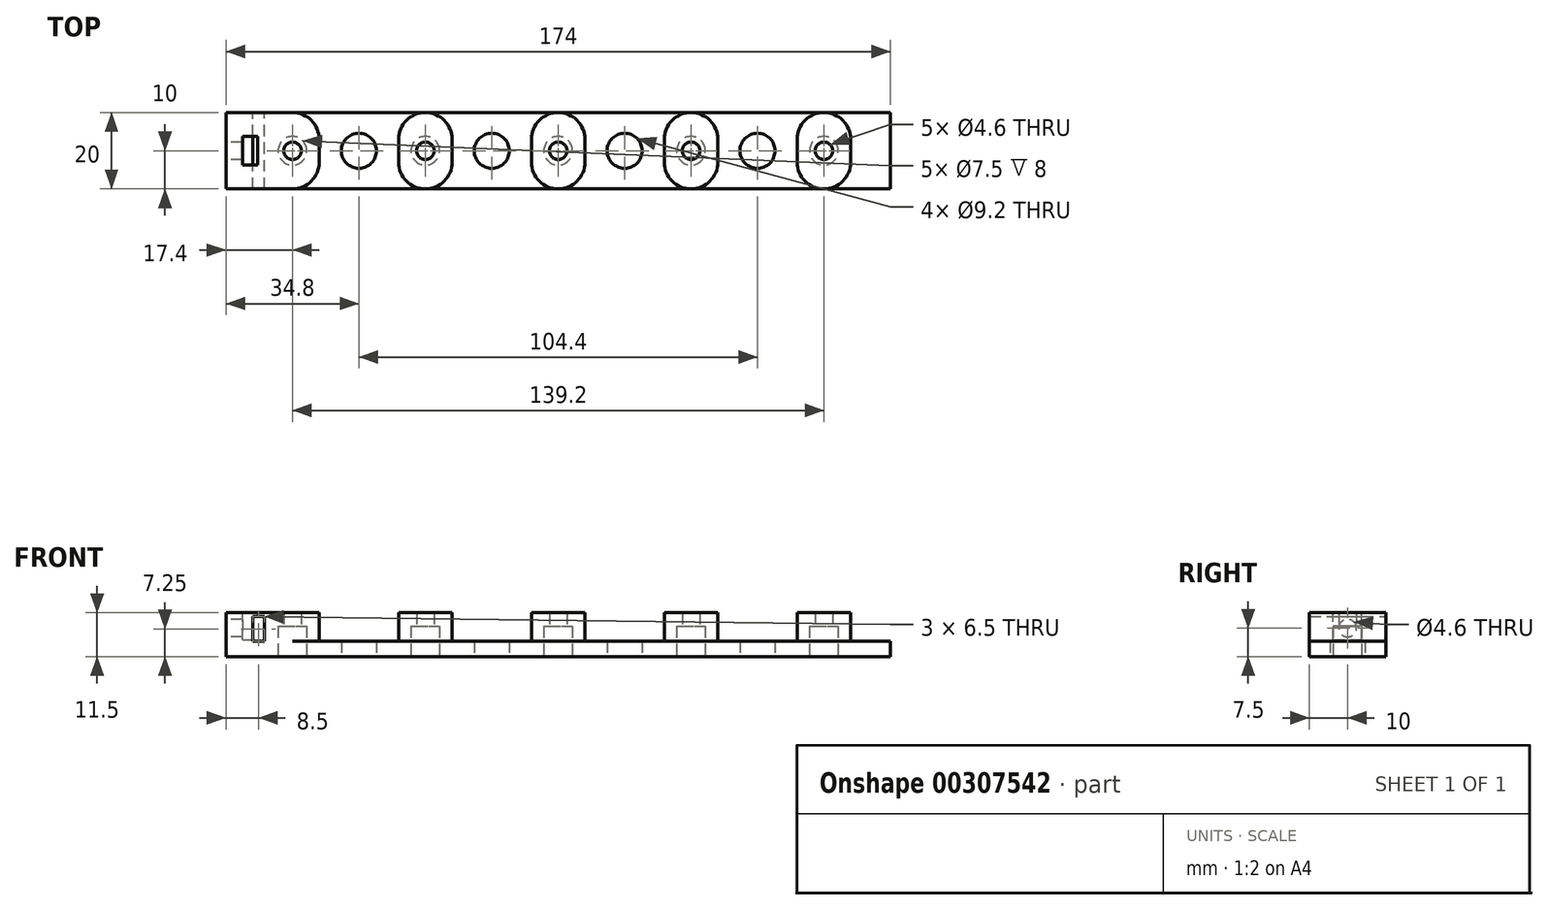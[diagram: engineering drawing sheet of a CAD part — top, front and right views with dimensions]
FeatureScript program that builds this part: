
annotation { "Feature Type Name" : "Feature", "Feature Type Description" : "" }
export const myFeature = defineFeature(function(context is Context, id is Id, definition is map)
    precondition{}
    {
        {
            var Q0;
            Q0=qCreatedBy(makeId("Top.planeOp"),FACE);
            var sketch = newSketch(context, id + "F0", { "sketchPlane" : qUnion([Q0])});
            skCircle(sketch, "E0", {"center": v(0, 0) * mm, "radius": 4.6 * mm});
            skCircle(sketch, "E1.1.0.0", {"center": v(34.8, 0) * mm, "radius": 4.6 * mm});
            skCircle(sketch, "E1.2.0.0", {"center": v(69.6, 0) * mm, "radius": 4.6 * mm});
            skCircle(sketch, "E1.3.0.0", {"center": v(104.4, 0) * mm, "radius": 4.6 * mm});
            skLineSegment(sketch, "E1.direction1", {"start": v(0, 0) * mm, "end": v(34.8, 0) * mm, "construction": true});
            skLineSegment(sketch, "E2.bottom", {"start": v(-34.8, 10) * mm, "end": v(139.2, 10) * mm});
            skLineSegment(sketch, "E2.top", {"start": v(-34.8, -10) * mm, "end": v(139.2, -10) * mm});
            skLineSegment(sketch, "E2.left", {"start": v(-34.8, 10) * mm, "end": v(-34.8, -10) * mm});
            skLineSegment(sketch, "E2.right", {"start": v(139.2, 10) * mm, "end": v(139.2, -10) * mm});
            skSolve(sketch);
        }
        {
            var Q0;
            Q0=makeQuery(id+"F0.imprint","IMPRINT",FACE,{"disambiguationData":[TD([[makeQuery(id+"F0.imprint","IMPRINT",EDGE,{"derivedFrom":sQuery(id+"F0.wireOp",EDGE,"E0")}),-1.0]])]});
            extrude(context, id + "F1", {"entities" : qUnion([Q0]), "depth" : 4 * mm, "offsetDistance" : 25 * mm});
        }
        {
            var Q0;
            Q0=makeQuery(id+"F1.opExtrude","CAP_FACE",FACE,{"disambiguationData":[OSD([sQuery(id+"F0.wireOp",EDGE,"E0"),sQuery(id+"F0.wireOp",EDGE,"E1.1.0.0"),sQuery(id+"F0.wireOp",EDGE,"E1.2.0.0"),sQuery(id+"F0.wireOp",EDGE,"E1.3.0.0"),sQuery(id+"F0.wireOp",EDGE,"E2.bottom"),sQuery(id+"F0.wireOp",EDGE,"E2.top"),sQuery(id+"F0.wireOp",EDGE,"E2.left"),sQuery(id+"F0.wireOp",EDGE,"E2.right")])],"isStart":false});
            var sketch = newSketch(context, id + "F2", { "sketchPlane" : qUnion([Q0])});
            skLineSegment(sketch, "E3.bottom", {"start": v(-24.4, 10) * mm, "end": v(-10.4, 10) * mm});
            skLineSegment(sketch, "E3.top", {"start": v(-24.4, -10) * mm, "end": v(-10.4, -10) * mm});
            skLineSegment(sketch, "E3.left", {"start": v(-24.4, 10) * mm, "end": v(-24.4, -10) * mm});
            skLineSegment(sketch, "E3.right", {"start": v(-10.4, 10) * mm, "end": v(-10.4, -10) * mm});
            skLineSegment(sketch, "E4.1.0.0", {"start": v(10.4, 10) * mm, "end": v(24.4, 10) * mm});
            skLineSegment(sketch, "E4.1.0.1", {"start": v(10.4, -10) * mm, "end": v(24.4, -10) * mm});
            skLineSegment(sketch, "E4.1.0.2", {"start": v(10.4, 10) * mm, "end": v(10.4, -10) * mm});
            skLineSegment(sketch, "E4.1.0.3", {"start": v(24.4, 10) * mm, "end": v(24.4, -10) * mm});
            skLineSegment(sketch, "E4.2.0.0", {"start": v(45.2, 10) * mm, "end": v(59.2, 10) * mm});
            skLineSegment(sketch, "E4.2.0.1", {"start": v(45.2, -10) * mm, "end": v(59.2, -10) * mm});
            skLineSegment(sketch, "E4.2.0.2", {"start": v(45.2, 10) * mm, "end": v(45.2, -10) * mm});
            skLineSegment(sketch, "E4.2.0.3", {"start": v(59.2, 10) * mm, "end": v(59.2, -10) * mm});
            skLineSegment(sketch, "E4.direction1", {"start": v(-24.4, -10) * mm, "end": v(10.4, -10) * mm, "construction": true});
            skLineSegment(sketch, "E5.0.3.0", {"start": v(80, 10) * mm, "end": v(94, 10) * mm});
            skLineSegment(sketch, "E5.3.3.0", {"start": v(80, -10) * mm, "end": v(94, -10) * mm});
            skLineSegment(sketch, "E5.6.3.0", {"start": v(80, 10) * mm, "end": v(80, -10) * mm});
            skLineSegment(sketch, "E5.9.3.0", {"start": v(94, 10) * mm, "end": v(94, -10) * mm});
            skLineSegment(sketch, "E5.0.4.0", {"start": v(114.8, 10) * mm, "end": v(128.8, 10) * mm});
            skLineSegment(sketch, "E5.3.4.0", {"start": v(114.8, -10) * mm, "end": v(128.8, -10) * mm});
            skLineSegment(sketch, "E5.6.4.0", {"start": v(114.8, 10) * mm, "end": v(114.8, -10) * mm});
            skLineSegment(sketch, "E5.9.4.0", {"start": v(128.8, 10) * mm, "end": v(128.8, -10) * mm});
            skSolve(sketch);
        }
        {
            var Q0;
            Q0 = qSketchRegion(id + "F2", true);
            extrude(context, id + "F3", {"entities" : qUnion([Q0]), "operationType" : NewBodyOperationType.ADD, "depth" : 7.5 * mm, "offsetDistance" : 25 * mm});
        }
        {
            var Q0;
            Q0=makeQuery(id+"F1.opExtrude","CAP_FACE",FACE,{"disambiguationData":[OSD([sQuery(id+"F0.wireOp",EDGE,"E0"),sQuery(id+"F0.wireOp",EDGE,"E1.1.0.0"),sQuery(id+"F0.wireOp",EDGE,"E1.2.0.0"),sQuery(id+"F0.wireOp",EDGE,"E1.3.0.0"),sQuery(id+"F0.wireOp",EDGE,"E2.bottom"),sQuery(id+"F0.wireOp",EDGE,"E2.top"),sQuery(id+"F0.wireOp",EDGE,"E2.left"),sQuery(id+"F0.wireOp",EDGE,"E2.right")])],"isStart":true});
            var sketch = newSketch(context, id + "F4", { "sketchPlane" : qUnion([Q0])});
            skPoint(sketch, "E6", {"position": v(-17.4, 0) * mm});
            skPoint(sketch, "E7.1.0.0", {"position": v(17.4, 0) * mm});
            skPoint(sketch, "E7.2.0.0", {"position": v(52.2, 0) * mm});
            skPoint(sketch, "E7.3.0.0", {"position": v(87, 0) * mm});
            skPoint(sketch, "E7.4.0.0", {"position": v(121.8, 0) * mm});
            skLineSegment(sketch, "E7.direction1", {"start": v(-17.4, 0) * mm, "end": v(17.4, 0) * mm, "construction": true});
            skSolve(sketch);
        }
        {
            var Q0;
            Q0=sQuery(id+"F4.wireOp",VERTEX,"E6");
            var Q1;
            Q1=sQuery(id+"F4.wireOp",VERTEX,"E7.1.0.0");
            var Q2;
            Q2=sQuery(id+"F4.wireOp",VERTEX,"E7.2.0.0");
            var Q3;
            Q3=sQuery(id+"F4.wireOp",VERTEX,"E7.3.0.0");
            var Q4;
            Q4=sQuery(id+"F4.wireOp",VERTEX,"E7.4.0.0");
            var Q5;
            Q5=makeQuery(id+"F1.opExtrude","SWEPT_BODY",BODY,{"disambiguationData":[OSD([sQuery(id+"F0.wireOp",EDGE,"E0"),sQuery(id+"F0.wireOp",EDGE,"E1.1.0.0"),sQuery(id+"F0.wireOp",EDGE,"E1.2.0.0"),sQuery(id+"F0.wireOp",EDGE,"E1.3.0.0"),sQuery(id+"F0.wireOp",EDGE,"E2.bottom"),sQuery(id+"F0.wireOp",EDGE,"E2.top"),sQuery(id+"F0.wireOp",EDGE,"E2.left"),sQuery(id+"F0.wireOp",EDGE,"E2.right")])]});
            hole(context, id + "F5", {"style" : HoleStyle.C_BORE, "endStyle" : HoleEndStyle.THROUGH, "holeDiameter" : 4.6 * mm, "cBoreDiameter" : 7.5 * mm, "cBoreDepth" : 8 * mm, "majorDiameter" : 5 * mm, "isTappedThrough" : true, "tappedDepth" : 12 * mm, "tapClearance" : 3, "startFromSketch" : true, "locations" : qUnion([Q0, Q1, Q2, Q3, Q4]), "scope" : qUnion([Q5])});
        }
        {
            var Q0;
            Q0=makeQuery(id+"F3.opExtrude","SWEPT_EDGE",EDGE,{"disambiguationData":[OSD([sQuery(id+"F0.wireOp",EDGE,"E2.bottom"),sQuery(id+"F2.wireOp",EDGE,"E3.bottom"),sQuery(id+"F2.wireOp",EDGE,"E3.right")])]});
            var Q1;
            Q1=makeQuery(id+"F3.opExtrude","SWEPT_EDGE",EDGE,{"disambiguationData":[OSD([sQuery(id+"F0.wireOp",EDGE,"E2.bottom"),sQuery(id+"F2.wireOp",EDGE,"E4.1.0.0"),sQuery(id+"F2.wireOp",EDGE,"E4.1.0.2")])]});
            var Q2;
            Q2=makeQuery(id+"F3.opExtrude","SWEPT_EDGE",EDGE,{"disambiguationData":[OSD([sQuery(id+"F0.wireOp",EDGE,"E2.bottom"),sQuery(id+"F2.wireOp",EDGE,"E4.1.0.0"),sQuery(id+"F2.wireOp",EDGE,"E4.1.0.3")])]});
            var Q3;
            Q3=makeQuery(id+"F3.opExtrude","SWEPT_EDGE",EDGE,{"disambiguationData":[OSD([sQuery(id+"F0.wireOp",EDGE,"E2.bottom"),sQuery(id+"F2.wireOp",EDGE,"E4.2.0.0"),sQuery(id+"F2.wireOp",EDGE,"E4.2.0.2")])]});
            var Q4;
            Q4=makeQuery(id+"F3.opExtrude","SWEPT_EDGE",EDGE,{"disambiguationData":[OSD([sQuery(id+"F0.wireOp",EDGE,"E2.bottom"),sQuery(id+"F2.wireOp",EDGE,"E4.2.0.0"),sQuery(id+"F2.wireOp",EDGE,"E4.2.0.3")])]});
            var Q5;
            Q5=makeQuery(id+"F3.opExtrude","SWEPT_EDGE",EDGE,{"disambiguationData":[OSD([sQuery(id+"F0.wireOp",EDGE,"E2.bottom"),sQuery(id+"F2.wireOp",EDGE,"E5.0.3.0"),sQuery(id+"F2.wireOp",EDGE,"E5.6.3.0")])]});
            var Q6;
            Q6=makeQuery(id+"F3.opExtrude","SWEPT_EDGE",EDGE,{"disambiguationData":[OSD([sQuery(id+"F0.wireOp",EDGE,"E2.bottom"),sQuery(id+"F2.wireOp",EDGE,"E5.0.3.0"),sQuery(id+"F2.wireOp",EDGE,"E5.9.3.0")])]});
            var Q7;
            Q7=makeQuery(id+"F3.opExtrude","SWEPT_EDGE",EDGE,{"disambiguationData":[OSD([sQuery(id+"F0.wireOp",EDGE,"E2.bottom"),sQuery(id+"F2.wireOp",EDGE,"E5.0.4.0"),sQuery(id+"F2.wireOp",EDGE,"E5.9.4.0")])]});
            var Q8;
            Q8=makeQuery(id+"F3.opExtrude","SWEPT_EDGE",EDGE,{"disambiguationData":[OSD([sQuery(id+"F0.wireOp",EDGE,"E2.bottom"),sQuery(id+"F2.wireOp",EDGE,"E5.0.4.0"),sQuery(id+"F2.wireOp",EDGE,"E5.6.4.0")])]});
            var Q9;
            Q9=makeQuery(id+"F3.opExtrude","SWEPT_EDGE",EDGE,{"disambiguationData":[OSD([sQuery(id+"F0.wireOp",EDGE,"E2.bottom"),sQuery(id+"F2.wireOp",EDGE,"E3.bottom"),sQuery(id+"F2.wireOp",EDGE,"E3.left")])]});
            var Q10;
            Q10=makeQuery(id+"F3.opExtrude","SWEPT_EDGE",EDGE,{"disambiguationData":[OSD([sQuery(id+"F0.wireOp",EDGE,"E2.top"),sQuery(id+"F2.wireOp",EDGE,"E3.top"),sQuery(id+"F2.wireOp",EDGE,"E3.left")])]});
            var Q11;
            Q11=makeQuery(id+"F3.opExtrude","SWEPT_EDGE",EDGE,{"disambiguationData":[OSD([sQuery(id+"F0.wireOp",EDGE,"E2.top"),sQuery(id+"F2.wireOp",EDGE,"E3.top"),sQuery(id+"F2.wireOp",EDGE,"E3.right")])]});
            var Q12;
            Q12=makeQuery(id+"F3.opExtrude","SWEPT_EDGE",EDGE,{"disambiguationData":[OSD([sQuery(id+"F0.wireOp",EDGE,"E2.top"),sQuery(id+"F2.wireOp",EDGE,"E4.1.0.1"),sQuery(id+"F2.wireOp",EDGE,"E4.1.0.2")])]});
            var Q13;
            Q13=makeQuery(id+"F3.opExtrude","SWEPT_EDGE",EDGE,{"disambiguationData":[OSD([sQuery(id+"F0.wireOp",EDGE,"E2.top"),sQuery(id+"F2.wireOp",EDGE,"E4.1.0.1"),sQuery(id+"F2.wireOp",EDGE,"E4.1.0.3")])]});
            var Q14;
            Q14=makeQuery(id+"F3.opExtrude","SWEPT_EDGE",EDGE,{"disambiguationData":[OSD([sQuery(id+"F0.wireOp",EDGE,"E2.top"),sQuery(id+"F2.wireOp",EDGE,"E4.2.0.1"),sQuery(id+"F2.wireOp",EDGE,"E4.2.0.2")])]});
            var Q15;
            Q15=makeQuery(id+"F3.opExtrude","SWEPT_EDGE",EDGE,{"disambiguationData":[OSD([sQuery(id+"F0.wireOp",EDGE,"E2.top"),sQuery(id+"F2.wireOp",EDGE,"E4.2.0.1"),sQuery(id+"F2.wireOp",EDGE,"E4.2.0.3")])]});
            var Q16;
            Q16=makeQuery(id+"F3.opExtrude","SWEPT_EDGE",EDGE,{"disambiguationData":[OSD([sQuery(id+"F0.wireOp",EDGE,"E2.top"),sQuery(id+"F2.wireOp",EDGE,"E5.3.3.0"),sQuery(id+"F2.wireOp",EDGE,"E5.6.3.0")])]});
            var Q17;
            Q17=makeQuery(id+"F3.opExtrude","SWEPT_EDGE",EDGE,{"disambiguationData":[OSD([sQuery(id+"F0.wireOp",EDGE,"E2.top"),sQuery(id+"F2.wireOp",EDGE,"E5.3.3.0"),sQuery(id+"F2.wireOp",EDGE,"E5.9.3.0")])]});
            var Q18;
            Q18=makeQuery(id+"F3.opExtrude","SWEPT_EDGE",EDGE,{"disambiguationData":[OSD([sQuery(id+"F0.wireOp",EDGE,"E2.top"),sQuery(id+"F2.wireOp",EDGE,"E5.3.4.0"),sQuery(id+"F2.wireOp",EDGE,"E5.6.4.0")])]});
            var Q19;
            Q19=makeQuery(id+"F3.opExtrude","SWEPT_EDGE",EDGE,{"disambiguationData":[OSD([sQuery(id+"F0.wireOp",EDGE,"E2.top"),sQuery(id+"F2.wireOp",EDGE,"E5.3.4.0"),sQuery(id+"F2.wireOp",EDGE,"E5.9.4.0")])]});
            fillet(context, id + "F6", {"entities" : qUnion([Q0, Q1, Q2, Q3, Q4, Q5, Q6, Q7, Q8, Q9, Q10, Q11, Q12, Q13, Q14, Q15, Q16, Q17, Q18, Q19]), "radius" : 7 * mm, "tangentPropagation" : true, "allowEdgeOverflow" : false});
        }
        {
            var Q0;
            {var subQ0=sQuery(id+"F0.wireOp",EDGE,"E2.left");var subQ1=sQuery(id+"F0.wireOp",EDGE,"E2.top");var subQ2=sQuery(id+"F0.wireOp",EDGE,"E2.bottom");Q0=makeQuery(id+"F3.boolean.opBoolean","SPLIT",FACE,{"disambiguationData":[TD([makeQuery(id+"F1.opExtrude","SWEPT_FACE",FACE,{"disambiguationData":[OSD([subQ0])]})])],"derivedFrom":makeQuery(id+"F1.opExtrude","CAP_FACE",FACE,{"disambiguationData":[OSD([sQuery(id+"F0.wireOp",EDGE,"E0"),sQuery(id+"F0.wireOp",EDGE,"E1.1.0.0"),sQuery(id+"F0.wireOp",EDGE,"E1.2.0.0"),sQuery(id+"F0.wireOp",EDGE,"E1.3.0.0"),subQ2,subQ1,subQ0,sQuery(id+"F0.wireOp",EDGE,"E2.right")])],"isStart":false})});}
            extrude(context, id + "F7", {"entities" : qUnion([Q0]), "operationType" : NewBodyOperationType.ADD, "depth" : 7.5 * mm, "offsetDistance" : 25 * mm});
        }
        {
            var Q0;
            {var subQ0=sQuery(id+"F0.wireOp",EDGE,"E2.bottom");Q0=makeQuery(id+"F7.boolean.opBoolean","MERGE",FACE,{"derivedFrom":[makeQuery(id+"F3.boolean.opBoolean","MERGE",FACE,{"derivedFrom":[makeQuery(id+"F1.opExtrude","SWEPT_FACE",FACE,{"disambiguationData":[OSD([subQ0])]}),makeQuery(id+"F3.opExtrude","SWEPT_FACE",FACE,{"disambiguationData":[OSD([sQuery(id+"F2.wireOp",EDGE,"E3.bottom")])]}),makeQuery(id+"F3.opExtrude","SWEPT_FACE",FACE,{"disambiguationData":[OSD([sQuery(id+"F2.wireOp",EDGE,"E4.1.0.0")])]}),makeQuery(id+"F3.opExtrude","SWEPT_FACE",FACE,{"disambiguationData":[OSD([sQuery(id+"F2.wireOp",EDGE,"E4.2.0.0")])]}),makeQuery(id+"F3.opExtrude","SWEPT_FACE",FACE,{"disambiguationData":[OSD([sQuery(id+"F2.wireOp",EDGE,"E5.0.3.0")])]}),makeQuery(id+"F3.opExtrude","SWEPT_FACE",FACE,{"disambiguationData":[OSD([sQuery(id+"F2.wireOp",EDGE,"E5.0.4.0")])]})]}),makeQuery(id+"F7.opExtrude","SWEPT_FACE",FACE,{"disambiguationData":[OSD([subQ0])]})]});}
            var sketch = newSketch(context, id + "F8", { "sketchPlane" : qUnion([Q0])});
            skLineSegment(sketch, "E8.bottom", {"start": v(24.8, 4) * mm, "end": v(27.8, 4) * mm});
            skLineSegment(sketch, "E8.top", {"start": v(24.8, 10.5) * mm, "end": v(27.8, 10.5) * mm});
            skLineSegment(sketch, "E8.left", {"start": v(24.8, 4) * mm, "end": v(24.8, 10.5) * mm});
            skLineSegment(sketch, "E8.right", {"start": v(27.8, 4) * mm, "end": v(27.8, 10.5) * mm});
            skSolve(sketch);
        }
        {
            var Q0;
            Q0 = qSketchRegion(id + "F8", true);
            extrude(context, id + "F9", {"entities" : qUnion([Q0]), "operationType" : NewBodyOperationType.REMOVE, "oppositeDirection" : true, "depth" : 25 * mm, "offsetDistance" : 25 * mm});
        }
        {
            var Q0;
            Q0=makeQuery(id+"F7.boolean.opBoolean","MERGE",FACE,{"derivedFrom":[makeQuery(id+"F3.opExtrude","CAP_FACE",FACE,{"disambiguationData":[OSD([sQuery(id+"F2.wireOp",EDGE,"E3.bottom"),sQuery(id+"F2.wireOp",EDGE,"E3.top"),sQuery(id+"F2.wireOp",EDGE,"E3.left"),sQuery(id+"F2.wireOp",EDGE,"E3.right")])],"isStart":false}),makeQuery(id+"F7.opExtrude","CAP_FACE",FACE,{"disambiguationData":[OSD([sQuery(id+"F0.wireOp",EDGE,"E0"),sQuery(id+"F0.wireOp",EDGE,"E1.1.0.0"),sQuery(id+"F0.wireOp",EDGE,"E1.2.0.0"),sQuery(id+"F0.wireOp",EDGE,"E1.3.0.0"),sQuery(id+"F0.wireOp",EDGE,"E2.bottom"),sQuery(id+"F0.wireOp",EDGE,"E2.top"),sQuery(id+"F0.wireOp",EDGE,"E2.left"),sQuery(id+"F0.wireOp",EDGE,"E2.right")])],"isStart":false})]});
            var sketch = newSketch(context, id + "F10", { "sketchPlane" : qUnion([Q0])});
            skLineSegment(sketch, "E9.bottom", {"start": v(-30.52, 3.75) * mm, "end": v(-26.52, 3.75) * mm});
            skLineSegment(sketch, "E9.top", {"start": v(-30.52, -3.75) * mm, "end": v(-26.52, -3.75) * mm});
            skLineSegment(sketch, "E9.left", {"start": v(-30.52, 3.75) * mm, "end": v(-30.52, -3.75) * mm});
            skLineSegment(sketch, "E9.right", {"start": v(-26.52, 3.75) * mm, "end": v(-26.52, -3.75) * mm});
            skSolve(sketch);
        }
        {
            var Q0;
            Q0 = qSketchRegion(id + "F10", true);
            extrude(context, id + "F11", {"entities" : qUnion([Q0]), "operationType" : NewBodyOperationType.REMOVE, "oppositeDirection" : true, "depth" : 7 * mm, "offsetDistance" : 25 * mm});
        }
        {
            var Q0;
            {var subQ0=sQuery(id+"F0.wireOp",EDGE,"E2.left");Q0=makeQuery(id+"F7.boolean.opBoolean","MERGE",FACE,{"derivedFrom":[makeQuery(id+"F1.opExtrude","SWEPT_FACE",FACE,{"disambiguationData":[OSD([subQ0])]}),makeQuery(id+"F7.opExtrude","SWEPT_FACE",FACE,{"disambiguationData":[OSD([subQ0])]})]});}
            var sketch = newSketch(context, id + "F12", { "sketchPlane" : qUnion([Q0])});
            skCircle(sketch, "E10", {"center": v(0, 7.5) * mm, "radius": 2.3 * mm});
            skSolve(sketch);
        }
        {
            var Q0;
            Q0 = qSketchRegion(id + "F12", true);
            extrude(context, id + "F13", {"entities" : qUnion([Q0]), "operationType" : NewBodyOperationType.REMOVE, "oppositeDirection" : true, "depth" : 10 * mm, "offsetDistance" : 25 * mm});
        }
    });
